# Revit family: VLGFS1501-xxxWS8xxBQPxxxx
name_source: partatom
category: Oprawy oświetleniowe
revit_build: Autodesk Revit 2017 (Build: 20190507_1515(x64)
units: mm (PartAtom-declared; Revit-internal decimal feet)

## family parameters
Numer OmniClass = 23.80.70.11
Obiekt nadrzędny = Powierzchnia
Punkt obliczania pomieszczeń = Nie
Tnij formami wycięć po wczytaniu = Nie
Typ części = Normalny
Tytuł OmniClass = Luminaries for Internal Lighting
Współdzielony = Nie
Wymiar okrągłego złącza = Użyj średnicy
Źródło światła = Tak

## types (20) — shared parameters
Emituj kształt widoczny w renderingu = Nie
Emituj z długości prostokąta = 94 mm  [stored 0.308399 ft]
Emituj z szerokości prostokąta = 1477 mm  [stored 4.8458 ft]
Filtr koloru = 16777215
Kod zespołu = D5020200
Lampa = LED
Odchylenie kierunku = 90.00°
Plik sieci fotometrycznej = VLGFS1501-5NDWS840BQP0750.IES
Producent = RIDI Leuchten GmbH
URL = www.ridi.de
Zmiana temperatury barwowej przyciemniania lampy = <Brak>
brand = RIDI
conformity mark = CE
electrical safety class = 1
height = 74 mm  [stored 0.242782 ft]
ingress protection (IP) code = IP54
length = 1500 mm  [stored 4.92126 ft]
nominal frequency = 50-60Hz
nominal voltage = 230
voltage type (AC, DC, UC) = AC
width = 97 mm  [stored 0.318241 ft]
zero-valued in all types: Domyślna rzędna

## per-type parameters (varying)
| type | Model | Obciążenie pozorne | rated input power | weight |
| VLGFS1501-5NDWS830BQP0350 | 1551261 | 30 VA | 30 | 3.02kg |
| VLGFS1501-7DAWS830BQP0350 | 1561261 | 30 VA | 30 | 2.883 kg |
| VLGFS1501-5NDWS830BQP0700 | 1551183 | 59 VA | 59 | 2.84 kg |
| VLGFS1501-7DAWS830BQP0700 | 1561183 | 59 VA | 59 | 2.84 kg |
| VLGFS1501-5NDWS830BQP0650-RF | 1551273 | 55 VA | 55 | 3.28kg |
| VLGFS1501-5NDWS840BQP0400 | 1551262 | 30 VA | 30 | 3.02kg |
| VLGFS1501-7DAWS840BQP0400 | 1561262 | 30 VA | 30 | 2.883 kg |
| VLGFS1501-5NDWS840BQP0750 | 1551180 | 59 VA | 59 | 2.84 kg |
| VLGFS1501-7DAWS840BQP0750 | 1561180 | 59 VA | 59 | 2.84 kg |
| VLGFS1501-5NDWS840BQP0700-RF | 1551274 | 55 VA | 55 | 3.28kg |
| VLGFS1501-5NDWS850BQP0400 | 1551263 | 30 VA | 30 | 3.02kg |
| VLGFS1501-7DAWS850BQP0400 | 1561263 | 30 VA | 30 | 2.883 kg |
| VLGFS1501-5NDWS850BQP0750 | 1551186 | 59 VA | 59 | 2.84 kg |
| VLGFS1501-7DAWS850BQP0750 | 1561186 | 59 VA | 59 | 2.84 kg |
| VLGFS1501-5NDWS850BQP0700-RF | 1551275 | 55 VA | 55 | 3.28 kg |
| VLGFS1501-5NDWS865BQP0400 | 1551264 | 30 VA | 30 | 3.02kg |
| VLGFS1501-7DAWS865BQP0400 | 1561264 | 30 VA | 30 | 2.883 kg |
| VLGFS1501-5NDWS865BQP0750 | 1551189 | 59 VA | 59 | 2.84 kg |
| VLGFS1501-7DAWS865BQP0750 | 1561189 | 59 VA | 59 | 2.84 kg |
| VLGFS1501-5NDWS865BQP0700-RF | 1551276 | 55 VA | 55 | 3.28 kg |

note: column(s) folded — value = type name in every type: product name

note: [stored X ft] marks values corroborated as IEEE doubles in the binary element streams (Revit-internal decimal feet)
